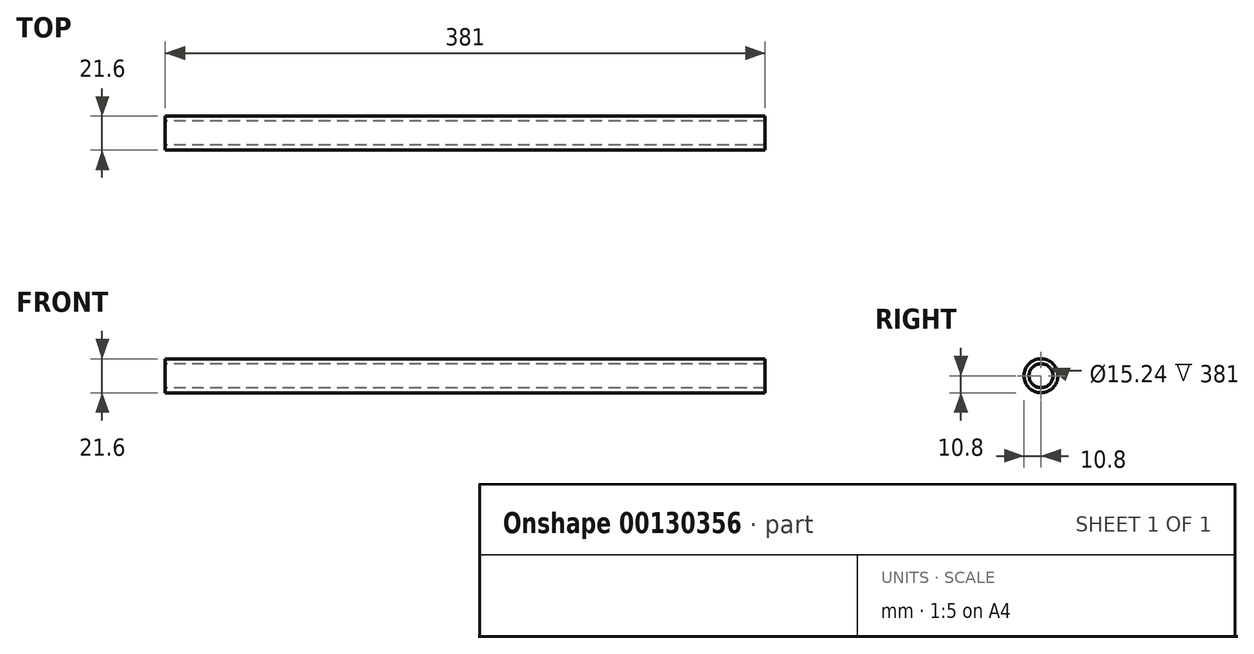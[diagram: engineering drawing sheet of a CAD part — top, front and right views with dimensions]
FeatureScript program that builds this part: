
annotation { "Feature Type Name" : "Feature", "Feature Type Description" : "" }
export const myFeature = defineFeature(function(context is Context, id is Id, definition is map)
    precondition{}
    {
        {
            var Q0;
            Q0=qCreatedBy(makeId("Right.planeOp"),FACE);
            var sketch = newSketch(context, id + "F0", { "sketchPlane" : qUnion([Q0])});
            skCircle(sketch, "E0", {"center": v(0, 0) * mm, "radius": 10.8 * mm});
            skSolve(sketch);
        }
        {
            var Q0;
            Q0=makeQuery(id+"F0.imprint","IMPRINT",FACE,{"disambiguationData":[TD([[makeQuery(id+"F0.imprint","IMPRINT",EDGE,{"derivedFrom":sQuery(id+"F0.wireOp",EDGE,"E0")}),1.0]])]});
            extrude(context, id + "F1", {"entities" : qUnion([Q0]), "depth" : 381 * mm});
        }
        {
            var Q0;
            Q0=makeQuery(id+"F1.opExtrude","CAP_FACE",FACE,{"disambiguationData":[OSD([sQuery(id+"F0.wireOp",EDGE,"E0")])],"isStart":false});
            var Q1;
            Q1=makeQuery(id+"F1.opExtrude","CAP_FACE",FACE,{"disambiguationData":[OSD([sQuery(id+"F0.wireOp",EDGE,"E0")])],"isStart":true});
            shell(context, id + "F2", {"entities" : qUnion([Q0, Q1]), "thickness" : 3.17 * mm});
        }
    });
